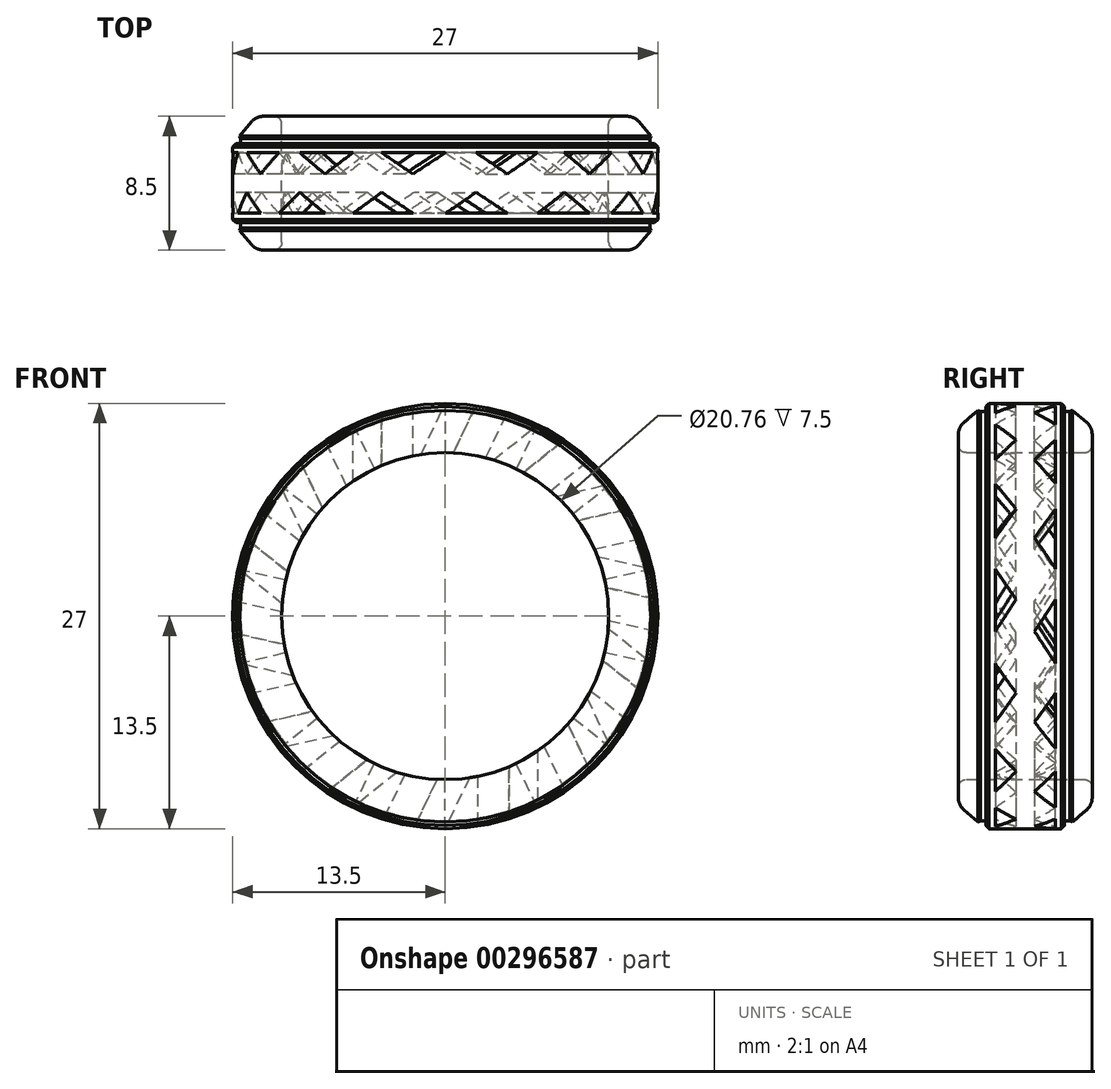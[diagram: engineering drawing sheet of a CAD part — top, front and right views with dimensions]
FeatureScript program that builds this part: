
annotation { "Feature Type Name" : "Feature", "Feature Type Description" : "" }
export const myFeature = defineFeature(function(context is Context, id is Id, definition is map)
    precondition{}
    {
        {
            var Q0;
            Q0=qCreatedBy(makeId("Front.planeOp"),FACE);
            var sketch = newSketch(context, id + "F0", { "sketchPlane" : qUnion([Q0])});
            skCircle(sketch, "E0", {"center": v(0, 0) * mm, "radius": 13.5 * mm});
            skCircle(sketch, "E1.0", {"center": v(0, 0) * mm, "radius": 10.38 * mm});
            skSolve(sketch);
        }
        {
            var Q0;
            Q0=makeQuery(id+"F0.imprint","IMPRINT",FACE,{"disambiguationData":[TD([[makeQuery(id+"F0.imprint","IMPRINT",EDGE,{"derivedFrom":sQuery(id+"F0.wireOp",EDGE,"E0")}),1.0]])]});
            extrude(context, id + "F1", {"entities" : qUnion([Q0]), "depth" : 8.5 * mm});
        }
        {
            var Q0;
            Q0=makeQuery(id+"F1.opExtrude","CAP_EDGE",EDGE,{"disambiguationData":[OSD([sQuery(id+"F0.wireOp",EDGE,"E0")])],"isStart":false});
            var Q1;
            Q1=makeQuery(id+"F1.opExtrude","CAP_EDGE",EDGE,{"disambiguationData":[OSD([sQuery(id+"F0.wireOp",EDGE,"E0")])],"isStart":true});
            chamfer(context, id + "F2", {"entities" : qUnion([Q0, Q1]), "chamferType" : ChamferType.TWO_OFFSETS, "width1" : 1.5 * mm, "oppositeDirection" : false, "width2" : 1.75 * mm, "tangentPropagation" : true});
        }
        {
            var Q0;
            Q0=qCreatedBy(makeId("Top.planeOp"),FACE);
            cPlane(context, id + "F3", {"entities" : qUnion([Q0]), "cplaneType" : CPlaneType.OFFSET, "offset" : 15.78 * mm, "width" : 150 * mm, "height" : 150 * mm});
        }
        {
            var Q0;
            Q0=qCreatedBy(id+"F3.planeOp",FACE);
            var sketch = newSketch(context, id + "F4", { "sketchPlane" : qUnion([Q0])});
            skLineSegment(sketch, "E2.bottom", {"start": v(-4.04, -2.32) * mm, "end": v(0, -2.32) * mm});
            skLineSegment(sketch, "E2.top", {"start": v(-4.04, -6.16) * mm, "end": v(-2.05, -6.16) * mm});
            skLineSegment(sketch, "E3", {"start": v(-4.04, -2.32) * mm, "end": v(-2.05, -3.66) * mm});
            skLineSegment(sketch, "E4", {"start": v(-2.05, -3.66) * mm, "end": v(0, -2.32) * mm});
            skLineSegment(sketch, "E5", {"start": v(-2.05, -6.16) * mm, "end": v(-4.04, -4.84) * mm});
            skLineSegment(sketch, "E6", {"start": v(0, -6.16) * mm, "end": v(2, -4.84) * mm});
            skLineSegment(sketch, "E7", {"start": v(2, -4.84) * mm, "end": v(4.08, -6.16) * mm});
            skLineSegment(sketch, "E8", {"start": v(2, -2.32) * mm, "end": v(4.08, -3.64) * mm});
            skLineSegment(sketch, "E9", {"start": v(-4.04, -4.84) * mm, "end": v(-5.84, -6.16) * mm});
            skLineSegment(sketch, "E10", {"start": v(-5.84, -6.16) * mm, "end": v(-4.04, -6.16) * mm});
            skLineSegment(sketch, "E11", {"start": v(4.08, -3.64) * mm, "end": v(6, -2.32) * mm});
            skLineSegment(sketch, "E12", {"start": v(6, -2.32) * mm, "end": v(4.08, -2.32) * mm});
            skLineSegment(sketch, "E13.trimOffspring", {"start": v(0, -6.16) * mm, "end": v(4.08, -6.16) * mm});
            skLineSegment(sketch, "E14.trimOffspring", {"start": v(2, -2.32) * mm, "end": v(4.08, -2.32) * mm});
            skSolve(sketch);
        }
        {
            var Q0;
            Q0=makeQuery(id+"F4.imprint","IMPRINT",FACE,{"disambiguationData":[TD([[makeQuery(id+"F4.imprint","IMPRINT",EDGE,{"derivedFrom":sQuery(id+"F4.wireOp",EDGE,"E2.top")}),1.0]])]});
            var Q1;
            Q1=makeQuery(id+"F4.imprint","IMPRINT",FACE,{"disambiguationData":[TD([[makeQuery(id+"F4.imprint","IMPRINT",EDGE,{"derivedFrom":sQuery(id+"F4.wireOp",EDGE,"E2.bottom")}),-1.0]])]});
            extrude(context, id + "F5", {"entities" : qUnion([Q0, Q1]), "operationType" : NewBodyOperationType.REMOVE, "oppositeDirection" : true, "depth" : 8 * mm, "hasDraft" : true, "draftAngle" : 0 * degree});
        }
        {
            var Q0;
            Q0=makeQuery(id+"F1.opExtrude","SWEPT_BODY",BODY,{"disambiguationData":[OSD([sQuery(id+"F0.wireOp",EDGE,"E0"),sQuery(id+"F0.wireOp",EDGE,"E1.0")])]});
            var Q1;
            Q1=makeQuery(id+"F5.boolean.opBoolean","COPY",FACE,{"derivedFrom":makeQuery(id+"F5.opExtrude","SWEPT_FACE",FACE,{"disambiguationData":[OSD([sQuery(id+"F4.wireOp",EDGE,"E9")])]})});
            var Q2;
            Q2=makeQuery(id+"F5.boolean.opBoolean","COPY",FACE,{"derivedFrom":makeQuery(id+"F5.opExtrude","SWEPT_FACE",FACE,{"disambiguationData":[OSD([sQuery(id+"F4.wireOp",EDGE,"E5")])]})});
            var Q3;
            Q3=makeQuery(id+"F5.boolean.opBoolean","COPY",FACE,{"derivedFrom":makeQuery(id+"F5.opExtrude","SWEPT_FACE",FACE,{"disambiguationData":[OSD([sQuery(id+"F4.wireOp",EDGE,"E2.top"),sQuery(id+"F4.wireOp",EDGE,"E10")])]})});
            var Q4;
            Q4=makeQuery(id+"F5.boolean.opBoolean","COPY",FACE,{"derivedFrom":makeQuery(id+"F5.opExtrude","SWEPT_FACE",FACE,{"disambiguationData":[OSD([sQuery(id+"F4.wireOp",EDGE,"E4")])]})});
            var Q5;
            Q5=makeQuery(id+"F5.boolean.opBoolean","COPY",FACE,{"derivedFrom":makeQuery(id+"F5.opExtrude","SWEPT_FACE",FACE,{"disambiguationData":[OSD([sQuery(id+"F4.wireOp",EDGE,"E3")])]})});
            var Q6;
            Q6=makeQuery(id+"F5.boolean.opBoolean","COPY",FACE,{"derivedFrom":makeQuery(id+"F5.opExtrude","SWEPT_FACE",FACE,{"disambiguationData":[OSD([sQuery(id+"F4.wireOp",EDGE,"E2.bottom")])]})});
            var Q7;
            Q7=makeQuery(id+"F5.boolean.opBoolean","COPY",FACE,{"derivedFrom":makeQuery(id+"F5.opExtrude","SWEPT_FACE",FACE,{"disambiguationData":[OSD([sQuery(id+"F4.wireOp",EDGE,"E7")])]})});
            var Q8;
            Q8=makeQuery(id+"F5.boolean.opBoolean","COPY",FACE,{"derivedFrom":makeQuery(id+"F5.opExtrude","SWEPT_FACE",FACE,{"disambiguationData":[OSD([sQuery(id+"F4.wireOp",EDGE,"E12"),sQuery(id+"F4.wireOp",EDGE,"E14.trimOffspring")])]})});
            var Q9;
            Q9=makeQuery(id+"F5.boolean.opBoolean","COPY",FACE,{"derivedFrom":makeQuery(id+"F5.opExtrude","SWEPT_FACE",FACE,{"disambiguationData":[OSD([sQuery(id+"F4.wireOp",EDGE,"E13.trimOffspring")])]})});
            var Q10;
            Q10=makeQuery(id+"F5.boolean.opBoolean","COPY",FACE,{"derivedFrom":makeQuery(id+"F5.opExtrude","SWEPT_FACE",FACE,{"disambiguationData":[OSD([sQuery(id+"F4.wireOp",EDGE,"E6")])]})});
            var Q11;
            Q11=makeQuery(id+"F5.boolean.opBoolean","COPY",FACE,{"derivedFrom":makeQuery(id+"F5.opExtrude","SWEPT_FACE",FACE,{"disambiguationData":[OSD([sQuery(id+"F4.wireOp",EDGE,"E8")])]})});
            var Q12;
            Q12=makeQuery(id+"F5.boolean.opBoolean","COPY",FACE,{"derivedFrom":makeQuery(id+"F5.opExtrude","SWEPT_FACE",FACE,{"disambiguationData":[OSD([sQuery(id+"F4.wireOp",EDGE,"E11")])]})});
            var Q13;
            Q13=makeQuery(id+"F1.opExtrude","SWEPT_FACE",FACE,{"disambiguationData":[OSD([sQuery(id+"F0.wireOp",EDGE,"E0")])]});
            circularPattern(context, id + "F6", {"patternType" : PatternType.FACE, "operationType" : NewBodyOperationType.REMOVE, "faces" : qUnion([Q1, Q2, Q3, Q4, Q5, Q6, Q7, Q8, Q9, Q10, Q11, Q12]), "axis" : qUnion([Q13]), "angle" : 360 * degree, "instanceCount" : 14, "equalSpace" : true});
        }
        {
            var Q0;
            Q0=qCreatedBy(makeId("Front.planeOp"),FACE);
            cPlane(context, id + "F7", {"entities" : qUnion([Q0]), "cplaneType" : CPlaneType.OFFSET, "offset" : 1.75 * mm, "width" : 150 * mm, "height" : 150 * mm});
        }
        {
            var Q0;
            Q0=qCreatedBy(id+"F7.planeOp",FACE);
            var sketch = newSketch(context, id + "F8", { "sketchPlane" : qUnion([Q0])});
            skCircle(sketch, "E15", {"center": v(0, 0) * mm, "radius": 13 * mm});
            skCircle(sketch, "E16", {"center": v(0, 0) * mm, "radius": 13.5 * mm});
            skSolve(sketch);
        }
        {
            var Q0;
            Q0 = qSketchRegion(id + "F8", true);
            extrude(context, id + "F9", {"entities" : qUnion([Q0]), "operationType" : NewBodyOperationType.REMOVE, "oppositeDirection" : true, "depth" : 0.25 * mm});
        }
        {
            var Q0;
            {var subQ0=sQuery(id+"F0.wireOp",EDGE,"E0");Q0=makeQuery(id+"F2.opChamfer","BLEND_EDGE",EDGE,{"blendedFrom":[makeQuery(id+"F1.opExtrude","CAP_EDGE",EDGE,{"disambiguationData":[OSD([subQ0])],"isStart":true}),makeQuery(id+"F1.opExtrude","CAP_FACE",FACE,{"disambiguationData":[OSD([subQ0,sQuery(id+"F0.wireOp",EDGE,"E1.0")])],"isStart":true})],"blendedInto":[makeQuery(id+"F1.opExtrude","CAP_FACE",FACE,{"disambiguationData":[OSD([subQ0,sQuery(id+"F0.wireOp",EDGE,"E1.0")])],"isStart":true})]});}
            fillet(context, id + "F10", {"entities" : qUnion([Q0]), "radius" : 1 * mm, "tangentPropagation" : true, "allowEdgeOverflow" : false});
        }
        {
            var Q0;
            Q0=makeQuery(id+"F1.opExtrude","CAP_FACE",FACE,{"disambiguationData":[OSD([sQuery(id+"F0.wireOp",EDGE,"E0"),sQuery(id+"F0.wireOp",EDGE,"E1.0")])],"isStart":false});
            cPlane(context, id + "F11", {"entities" : qUnion([Q0]), "cplaneType" : CPlaneType.OFFSET, "offset" : 1.75 * mm, "oppositeDirection" : true, "width" : 150 * mm, "height" : 150 * mm});
        }
        {
            var Q0;
            Q0=qCreatedBy(id+"F11.planeOp",FACE);
            var sketch = newSketch(context, id + "F12", { "sketchPlane" : qUnion([Q0])});
            skCircle(sketch, "E17", {"center": v(0, 0) * mm, "radius": 13 * mm});
            skCircle(sketch, "E18", {"center": v(0, 0) * mm, "radius": 13.5 * mm});
            skSolve(sketch);
        }
        {
            var Q0;
            Q0 = qSketchRegion(id + "F12", true);
            extrude(context, id + "F13", {"entities" : qUnion([Q0]), "operationType" : NewBodyOperationType.REMOVE, "depth" : 0.25 * mm});
        }
        {
            var Q0;
            {var subQ0=sQuery(id+"F0.wireOp",EDGE,"E0");Q0=makeQuery(id+"F2.opChamfer","BLEND_EDGE",EDGE,{"blendedFrom":[makeQuery(id+"F1.opExtrude","CAP_EDGE",EDGE,{"disambiguationData":[OSD([subQ0])],"isStart":false}),makeQuery(id+"F1.opExtrude","CAP_FACE",FACE,{"disambiguationData":[OSD([subQ0,sQuery(id+"F0.wireOp",EDGE,"E1.0")])],"isStart":false})],"blendedInto":[makeQuery(id+"F1.opExtrude","CAP_FACE",FACE,{"disambiguationData":[OSD([subQ0,sQuery(id+"F0.wireOp",EDGE,"E1.0")])],"isStart":false})]});}
            fillet(context, id + "F14", {"entities" : qUnion([Q0]), "radius" : 1 * mm, "tangentPropagation" : true, "allowEdgeOverflow" : false});
        }
        {
            var Q0;
            Q0=makeQuery(id+"F1.opExtrude","CAP_EDGE",EDGE,{"disambiguationData":[OSD([sQuery(id+"F0.wireOp",EDGE,"E1.0")])],"isStart":false});
            fillet(context, id + "F15", {"entities" : qUnion([Q0]), "radius" : 0.5 * mm, "tangentPropagation" : true, "allowEdgeOverflow" : false});
        }
        {
            var Q0;
            Q0=makeQuery(id+"F1.opExtrude","CAP_EDGE",EDGE,{"disambiguationData":[OSD([sQuery(id+"F0.wireOp",EDGE,"E1.0")])],"isStart":true});
            fillet(context, id + "F16", {"entities" : qUnion([Q0]), "radius" : 0.5 * mm, "tangentPropagation" : true, "allowEdgeOverflow" : false});
        }
        {
            var Q0;
            {var subQ0=sQuery(id+"F0.wireOp",EDGE,"E0");Q0=makeQuery(id+"F9.boolean.opBoolean","MERGE",EDGE,{"derivedFrom":[makeQuery(id+"F2.opChamfer","BLEND_EDGE",EDGE,{"blendedFrom":[makeQuery(id+"F1.opExtrude","CAP_EDGE",EDGE,{"disambiguationData":[OSD([subQ0])],"isStart":true}),makeQuery(id+"F1.opExtrude","SWEPT_FACE",FACE,{"disambiguationData":[OSD([subQ0])]})],"blendedInto":[makeQuery(id+"F1.opExtrude","SWEPT_FACE",FACE,{"disambiguationData":[OSD([subQ0])]})]}),makeQuery(id+"F9.opExtrude","CAP_EDGE",EDGE,{"disambiguationData":[OSD([sQuery(id+"F8.wireOp",EDGE,"E16")])],"isStart":true})]});}
            var Q1;
            {var subQ0=sQuery(id+"F0.wireOp",EDGE,"E0");Q1=makeQuery(id+"F13.boolean.opBoolean","MERGE",EDGE,{"derivedFrom":[makeQuery(id+"F2.opChamfer","BLEND_EDGE",EDGE,{"blendedFrom":[makeQuery(id+"F1.opExtrude","CAP_EDGE",EDGE,{"disambiguationData":[OSD([subQ0])],"isStart":false}),makeQuery(id+"F1.opExtrude","SWEPT_FACE",FACE,{"disambiguationData":[OSD([subQ0])]})],"blendedInto":[makeQuery(id+"F1.opExtrude","SWEPT_FACE",FACE,{"disambiguationData":[OSD([subQ0])]})]}),makeQuery(id+"F13.opExtrude","CAP_EDGE",EDGE,{"disambiguationData":[OSD([sQuery(id+"F12.wireOp",EDGE,"E18")])],"isStart":true})]});}
            chamfer(context, id + "F17", {"entities" : qUnion([Q0, Q1]), "width" : 0.2 * mm});
        }
        {
            var Q0;
            {var subQ0=sQuery(id+"F0.wireOp",EDGE,"E0");Q0=makeQuery(id+"F13.boolean.opBoolean","INTERSECT",EDGE,{"derivedFrom":[makeQuery(id+"F2.opChamfer","BLEND_FACE",FACE,{"disambiguationData":[OSD([subQ0]),TDD([makeQuery(id+"F1.opExtrude","CAP_EDGE",EDGE,{"disambiguationData":[OSD([subQ0])],"isStart":false})])]}),makeQuery(id+"F13.opExtrude","CAP_FACE",FACE,{"disambiguationData":[OSD([sQuery(id+"F12.wireOp",EDGE,"E17"),sQuery(id+"F12.wireOp",EDGE,"E18")])],"isStart":false})]});}
            var Q1;
            {var subQ0=sQuery(id+"F0.wireOp",EDGE,"E0");Q1=makeQuery(id+"F2.opChamfer","BLEND_FACE",FACE,{"disambiguationData":[OSD([subQ0]),TDD([makeQuery(id+"F1.opExtrude","CAP_EDGE",EDGE,{"disambiguationData":[OSD([subQ0])],"isStart":true})])]});}
            chamfer(context, id + "F18", {"entities" : qUnion([Q0, Q1]), "width" : 0.15 * mm, "tangentPropagation" : true});
        }
    });
